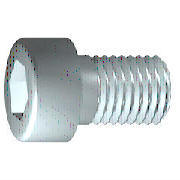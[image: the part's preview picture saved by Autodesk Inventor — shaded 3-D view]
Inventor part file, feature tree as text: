
AUTODESK INVENTOR PART (.ipt)
format: ipt  version: 2018 (Build 220112000, 112)  size: 180,224 bytes
history: native  units: mm (DEFAULTED — no unit token found)
features: sketch x2, extrude x1, plane x1, fillet x1
ambient origin geometry x7: Origin, YZ Plane, XY Plane, X Axis, Y Axis, Z Axis, Center Point
bodies: Solid1 (feature_tree), Body (feature_tree)
feature tree (5):
  extrude  "Slot"  Depth=3.0mm
  plane  "Work Plane1"
  fillet  "Fillet2"  Radius=3.0mm
  sketch  "Sketch1"  dims[d1=18.0mm d2=0.306825mm d3=3.0mm]
  sketch  "Sketch2"  dims[d4=1.5mm d5=60.0deg d6=3.0mm d7=3.0mm d8=2.886751mm d9=5.5mm d10=90.0deg d11=10.0mm d12=0.0mm d13=18.0mm d14=0.0mm d15=0.306725mm d16=0.306725mm d17=0.3mm d19=0.0mm d26=55.0mm d27=45.0deg d28=0.0mm d29=0.0mm d30=0.1mm]
